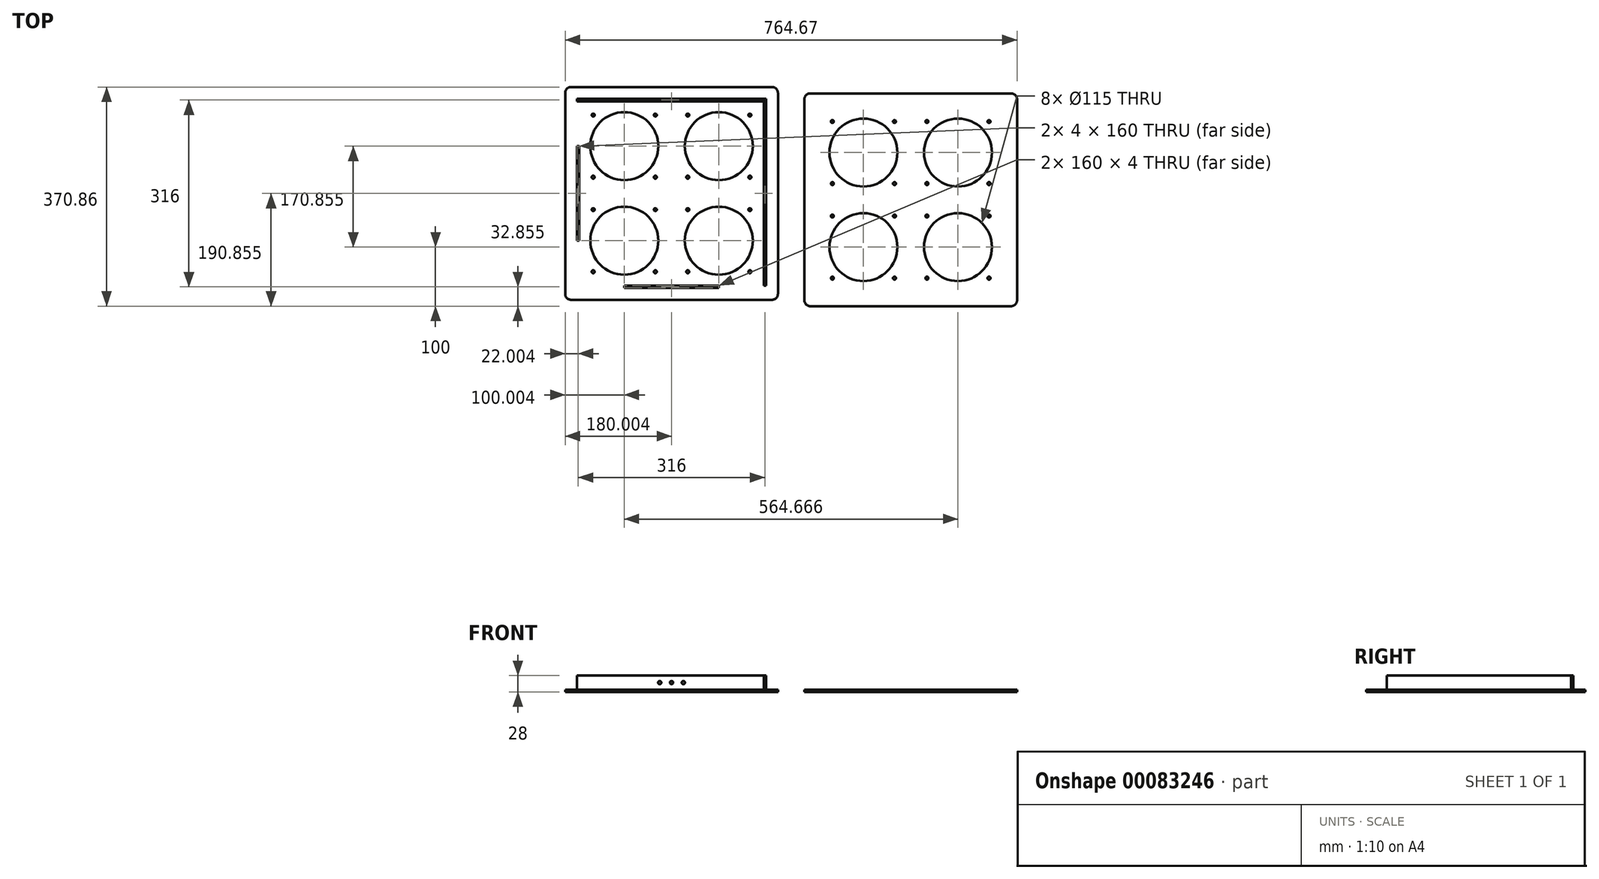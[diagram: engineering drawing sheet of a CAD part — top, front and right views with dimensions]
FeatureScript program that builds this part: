
annotation { "Feature Type Name" : "Feature", "Feature Type Description" : "" }
export const myFeature = defineFeature(function(context is Context, id is Id, definition is map)
    precondition{}
    {
        {
            var Q0;
            Q0=qCreatedBy(makeId("Top.planeOp"),FACE);
            var sketch = newSketch(context, id + "F0", { "sketchPlane" : qUnion([Q0])});
            skLineSegment(sketch, "E0.bottom", {"start": v(-180.3, 193.62) * mm, "end": v(159.7, 193.62) * mm});
            skLineSegment(sketch, "E0.top", {"start": v(-180.3, -166.38) * mm, "end": v(159.7, -166.38) * mm});
            skLineSegment(sketch, "E0.left", {"start": v(-190.3, 183.62) * mm, "end": v(-190.3, -156.38) * mm});
            skLineSegment(sketch, "E0.right", {"start": v(169.7, 183.62) * mm, "end": v(169.7, -156.38) * mm});
            skPoint(sketch, "E1.visualSharp", {"position": v(-190.3, 193.62) * mm});
            skArc(sketch, "E1.filletArc", {"start": v(-180.3, 193.62) * mm, "mid": v(-187.38, 190.69) * mm, "end": v(-190.3, 183.62) * mm});
            skPoint(sketch, "E2.visualSharp", {"position": v(169.7, 193.62) * mm});
            skArc(sketch, "E2.filletArc", {"start": v(169.7, 183.62) * mm, "mid": v(166.76, 190.69) * mm, "end": v(159.7, 193.62) * mm});
            skPoint(sketch, "E3.visualSharp", {"position": v(169.7, -166.38) * mm});
            skArc(sketch, "E3.filletArc", {"start": v(159.7, -166.38) * mm, "mid": v(166.76, -163.46) * mm, "end": v(169.7, -156.38) * mm});
            skPoint(sketch, "E4.visualSharp", {"position": v(-190.3, -166.38) * mm});
            skArc(sketch, "E4.filletArc", {"start": v(-190.3, -156.38) * mm, "mid": v(-187.38, -163.46) * mm, "end": v(-180.3, -166.38) * mm});
            skLineSegment(sketch, "E5", {"start": v(-190.3, 93.62) * mm, "end": v(169.7, 93.62) * mm, "construction": true});
            skLineSegment(sketch, "E6", {"start": v(-190.3, -66.38) * mm, "end": v(169.7, -66.38) * mm, "construction": true});
            skLineSegment(sketch, "E7", {"start": v(-90.3, 193.62) * mm, "end": v(-90.3, -166.38) * mm, "construction": true});
            skLineSegment(sketch, "E8", {"start": v(69.7, 193.62) * mm, "end": v(69.7, -166.38) * mm, "construction": true});
            skCircle(sketch, "E9", {"center": v(-90.3, 93.62) * mm, "radius": 57.5 * mm});
            skCircle(sketch, "E10", {"center": v(-90.3, 93.62) * mm, "radius": 74.3 * mm, "construction": true});
            skLineSegment(sketch, "E11.bottom", {"start": v(-30.3, 153.62) * mm, "end": v(-150.3, 153.62) * mm, "construction": true});
            skLineSegment(sketch, "E11.top", {"start": v(-30.3, 33.62) * mm, "end": v(-150.3, 33.62) * mm, "construction": true});
            skLineSegment(sketch, "E11.left", {"start": v(-30.3, 153.62) * mm, "end": v(-30.3, 33.62) * mm, "construction": true});
            skLineSegment(sketch, "E11.right", {"start": v(-150.3, 153.62) * mm, "end": v(-150.3, 33.62) * mm, "construction": true});
            skLineSegment(sketch, "E12", {"start": v(-150.3, 153.62) * mm, "end": v(-30.3, 33.62) * mm, "construction": true});
            skLineSegment(sketch, "E13", {"start": v(-150.3, 33.62) * mm, "end": v(-30.3, 153.62) * mm, "construction": true});
            skPoint(sketch, "E14", {"position": v(-142.84, 146.15) * mm});
            skPoint(sketch, "E15", {"position": v(-37.77, 146.15) * mm});
            skPoint(sketch, "E16", {"position": v(-37.77, 41.08) * mm});
            skPoint(sketch, "E17", {"position": v(-142.84, 41.08) * mm});
            skCircle(sketch, "E18", {"center": v(-142.84, 146.15) * mm, "radius": 2.5 * mm});
            skCircle(sketch, "E19", {"center": v(-37.77, 146.15) * mm, "radius": 2.5 * mm});
            skCircle(sketch, "E20", {"center": v(-37.77, 41.08) * mm, "radius": 2.5 * mm});
            skCircle(sketch, "E21", {"center": v(-142.84, 41.08) * mm, "radius": 2.5 * mm});
            skLineSegment(sketch, "E22", {"start": v(-190.3, 13.62) * mm, "end": v(169.7, 13.62) * mm, "construction": true});
            skLineSegment(sketch, "E23", {"start": v(-10.3, 193.62) * mm, "end": v(-10.3, -166.38) * mm, "construction": true});
            skLineSegment(sketch, "E24.0.1.0", {"start": v(-30.3, -6.38) * mm, "end": v(-150.3, -6.38) * mm, "construction": true});
            skLineSegment(sketch, "E24.0.1.1", {"start": v(-30.3, -126.38) * mm, "end": v(-150.3, -126.38) * mm, "construction": true});
            skPoint(sketch, "E24.0.1.2", {"position": v(-90.3, -66.38) * mm});
            skCircle(sketch, "E24.0.1.3", {"center": v(-90.3, -66.38) * mm, "radius": 57.5 * mm});
            skPoint(sketch, "E24.0.1.4", {"position": v(-37.77, -13.85) * mm});
            skCircle(sketch, "E24.0.1.5", {"center": v(-90.3, -66.38) * mm, "radius": 74.3 * mm, "construction": true});
            skLineSegment(sketch, "E24.0.1.6", {"start": v(-30.3, -6.38) * mm, "end": v(-30.3, -126.38) * mm, "construction": true});
            skLineSegment(sketch, "E24.0.1.7", {"start": v(-150.3, -6.38) * mm, "end": v(-30.3, -126.38) * mm, "construction": true});
            skLineSegment(sketch, "E24.0.1.8", {"start": v(-150.3, -6.38) * mm, "end": v(-150.3, -126.38) * mm, "construction": true});
            skLineSegment(sketch, "E24.0.1.9", {"start": v(-150.3, -126.38) * mm, "end": v(-30.3, -6.38) * mm, "construction": true});
            skPoint(sketch, "E24.0.1.10", {"position": v(-142.84, -118.92) * mm});
            skPoint(sketch, "E24.0.1.11", {"position": v(-142.84, -13.85) * mm});
            skPoint(sketch, "E24.0.1.12", {"position": v(-37.77, -118.92) * mm});
            skPoint(sketch, "E24.0.1.13", {"position": v(-90.3, -66.38) * mm});
            skCircle(sketch, "E24.0.1.14", {"center": v(-142.84, -118.92) * mm, "radius": 2.5 * mm});
            skCircle(sketch, "E24.0.1.15", {"center": v(-37.77, -118.92) * mm, "radius": 2.5 * mm});
            skCircle(sketch, "E24.0.1.16", {"center": v(-142.84, -13.85) * mm, "radius": 2.5 * mm});
            skCircle(sketch, "E24.0.1.17", {"center": v(-37.77, -13.85) * mm, "radius": 2.5 * mm});
            skLineSegment(sketch, "E24.1.0.0", {"start": v(129.7, 153.62) * mm, "end": v(9.7, 153.62) * mm, "construction": true});
            skLineSegment(sketch, "E24.1.0.1", {"start": v(129.7, 33.62) * mm, "end": v(9.7, 33.62) * mm, "construction": true});
            skPoint(sketch, "E24.1.0.2", {"position": v(69.7, 93.62) * mm});
            skCircle(sketch, "E24.1.0.3", {"center": v(69.7, 93.62) * mm, "radius": 57.5 * mm});
            skPoint(sketch, "E24.1.0.4", {"position": v(122.23, 146.15) * mm});
            skCircle(sketch, "E24.1.0.5", {"center": v(69.7, 93.62) * mm, "radius": 74.3 * mm, "construction": true});
            skLineSegment(sketch, "E24.1.0.6", {"start": v(129.7, 153.62) * mm, "end": v(129.7, 33.62) * mm, "construction": true});
            skLineSegment(sketch, "E24.1.0.7", {"start": v(9.7, 153.62) * mm, "end": v(129.7, 33.62) * mm, "construction": true});
            skLineSegment(sketch, "E24.1.0.8", {"start": v(9.7, 153.62) * mm, "end": v(9.7, 33.62) * mm, "construction": true});
            skLineSegment(sketch, "E24.1.0.9", {"start": v(9.7, 33.62) * mm, "end": v(129.7, 153.62) * mm, "construction": true});
            skPoint(sketch, "E24.1.0.10", {"position": v(17.16, 41.08) * mm});
            skPoint(sketch, "E24.1.0.11", {"position": v(17.16, 146.15) * mm});
            skPoint(sketch, "E24.1.0.12", {"position": v(122.23, 41.08) * mm});
            skPoint(sketch, "E24.1.0.13", {"position": v(69.7, 93.62) * mm});
            skCircle(sketch, "E24.1.0.14", {"center": v(17.16, 41.08) * mm, "radius": 2.5 * mm});
            skCircle(sketch, "E24.1.0.15", {"center": v(122.23, 41.08) * mm, "radius": 2.5 * mm});
            skCircle(sketch, "E24.1.0.16", {"center": v(17.16, 146.15) * mm, "radius": 2.5 * mm});
            skCircle(sketch, "E24.1.0.17", {"center": v(122.23, 146.15) * mm, "radius": 2.5 * mm});
            skLineSegment(sketch, "E24.1.1.0", {"start": v(129.7, -6.38) * mm, "end": v(9.7, -6.38) * mm, "construction": true});
            skLineSegment(sketch, "E24.1.1.1", {"start": v(129.7, -126.38) * mm, "end": v(9.7, -126.38) * mm, "construction": true});
            skPoint(sketch, "E24.1.1.2", {"position": v(69.7, -66.38) * mm});
            skCircle(sketch, "E24.1.1.3", {"center": v(69.7, -66.38) * mm, "radius": 57.5 * mm});
            skPoint(sketch, "E24.1.1.4", {"position": v(122.23, -13.85) * mm});
            skCircle(sketch, "E24.1.1.5", {"center": v(69.7, -66.38) * mm, "radius": 74.3 * mm, "construction": true});
            skLineSegment(sketch, "E24.1.1.6", {"start": v(129.7, -6.38) * mm, "end": v(129.7, -126.38) * mm, "construction": true});
            skLineSegment(sketch, "E24.1.1.7", {"start": v(9.7, -6.38) * mm, "end": v(129.7, -126.38) * mm, "construction": true});
            skLineSegment(sketch, "E24.1.1.8", {"start": v(9.7, -6.38) * mm, "end": v(9.7, -126.38) * mm, "construction": true});
            skLineSegment(sketch, "E24.1.1.9", {"start": v(9.7, -126.38) * mm, "end": v(129.7, -6.38) * mm, "construction": true});
            skPoint(sketch, "E24.1.1.10", {"position": v(17.16, -118.92) * mm});
            skPoint(sketch, "E24.1.1.11", {"position": v(17.16, -13.85) * mm});
            skPoint(sketch, "E24.1.1.12", {"position": v(122.23, -118.92) * mm});
            skPoint(sketch, "E24.1.1.13", {"position": v(69.7, -66.38) * mm});
            skCircle(sketch, "E24.1.1.14", {"center": v(17.16, -118.92) * mm, "radius": 2.5 * mm});
            skCircle(sketch, "E24.1.1.15", {"center": v(122.23, -118.92) * mm, "radius": 2.5 * mm});
            skCircle(sketch, "E24.1.1.16", {"center": v(17.16, -13.85) * mm, "radius": 2.5 * mm});
            skCircle(sketch, "E24.1.1.17", {"center": v(122.23, -13.85) * mm, "radius": 2.5 * mm});
            skLineSegment(sketch, "E24.direction1", {"start": v(-150.3, 33.62) * mm, "end": v(9.7, 33.62) * mm, "construction": true});
            skLineSegment(sketch, "E24.direction2", {"start": v(-150.3, 33.62) * mm, "end": v(-150.3, -126.38) * mm, "construction": true});
            skLineSegment(sketch, "E25", {"start": v(-166.3, 93.62) * mm, "end": v(-166.3, -66.38) * mm});
            skLineSegment(sketch, "E26", {"start": v(-170.3, 93.62) * mm, "end": v(-170.3, -66.38) * mm});
            skLineSegment(sketch, "E27", {"start": v(-170.3, 93.62) * mm, "end": v(-166.3, 93.62) * mm});
            skLineSegment(sketch, "E28", {"start": v(-170.3, -66.38) * mm, "end": v(-166.3, -66.38) * mm});
            skLineSegment(sketch, "E29.bottom", {"start": v(-90.3, -146.38) * mm, "end": v(69.7, -146.38) * mm});
            skLineSegment(sketch, "E29.top", {"start": v(-90.3, -142.38) * mm, "end": v(69.7, -142.38) * mm});
            skLineSegment(sketch, "E29.left", {"start": v(-90.3, -146.38) * mm, "end": v(-90.3, -142.38) * mm});
            skLineSegment(sketch, "E29.right", {"start": v(69.7, -146.38) * mm, "end": v(69.7, -142.38) * mm});
            skLineSegment(sketch, "E30.MirrorCS", {"start": v(-90.3, 173.62) * mm, "end": v(-90.3, 169.62) * mm});
            skLineSegment(sketch, "E31.MirrorCS", {"start": v(69.7, 173.62) * mm, "end": v(69.7, 169.62) * mm});
            skLineSegment(sketch, "E32.MirrorCS", {"start": v(-90.3, 173.62) * mm, "end": v(69.7, 173.62) * mm});
            skLineSegment(sketch, "E33.MirrorCS", {"start": v(-90.3, 169.62) * mm, "end": v(69.7, 169.62) * mm});
            skLineSegment(sketch, "E34.MirrorCS", {"start": v(149.7, -66.38) * mm, "end": v(145.7, -66.38) * mm});
            skLineSegment(sketch, "E35.MirrorCS", {"start": v(149.7, 93.62) * mm, "end": v(145.7, 93.62) * mm});
            skLineSegment(sketch, "E36.MirrorCS", {"start": v(149.7, 93.62) * mm, "end": v(149.7, -66.38) * mm});
            skLineSegment(sketch, "E37.MirrorCS", {"start": v(145.7, 93.62) * mm, "end": v(145.7, -66.38) * mm});
            skLineSegment(sketch, "E38.bottom", {"start": v(224.36, 182.76) * mm, "end": v(564.36, 182.76) * mm});
            skLineSegment(sketch, "E38.top", {"start": v(224.36, -177.24) * mm, "end": v(564.36, -177.24) * mm});
            skLineSegment(sketch, "E38.left", {"start": v(214.36, 172.76) * mm, "end": v(214.36, -167.24) * mm});
            skLineSegment(sketch, "E38.right", {"start": v(574.36, 172.76) * mm, "end": v(574.36, -167.24) * mm});
            skPoint(sketch, "E39.visualSharp", {"position": v(214.36, 182.76) * mm});
            skArc(sketch, "E39.filletArc", {"start": v(224.36, 182.76) * mm, "mid": v(217.29, 179.83) * mm, "end": v(214.36, 172.76) * mm});
            skPoint(sketch, "E40.visualSharp", {"position": v(574.36, 182.76) * mm});
            skArc(sketch, "E40.filletArc", {"start": v(574.36, 172.76) * mm, "mid": v(571.43, 179.83) * mm, "end": v(564.36, 182.76) * mm});
            skPoint(sketch, "E41.visualSharp", {"position": v(574.36, -177.24) * mm});
            skArc(sketch, "E41.filletArc", {"start": v(564.36, -177.24) * mm, "mid": v(571.43, -174.31) * mm, "end": v(574.36, -167.24) * mm});
            skPoint(sketch, "E42.visualSharp", {"position": v(214.36, -177.24) * mm});
            skArc(sketch, "E42.filletArc", {"start": v(214.36, -167.24) * mm, "mid": v(217.29, -174.31) * mm, "end": v(224.36, -177.24) * mm});
            skLineSegment(sketch, "E43", {"start": v(214.36, 82.76) * mm, "end": v(574.36, 82.76) * mm, "construction": true});
            skLineSegment(sketch, "E44", {"start": v(214.36, -77.24) * mm, "end": v(574.36, -77.24) * mm, "construction": true});
            skLineSegment(sketch, "E45", {"start": v(314.36, 182.76) * mm, "end": v(314.36, -177.24) * mm, "construction": true});
            skLineSegment(sketch, "E46", {"start": v(474.36, 182.76) * mm, "end": v(474.36, -177.24) * mm, "construction": true});
            skCircle(sketch, "E47", {"center": v(314.36, 82.76) * mm, "radius": 57.5 * mm});
            skCircle(sketch, "E48", {"center": v(314.36, 82.76) * mm, "radius": 74.3 * mm, "construction": true});
            skLineSegment(sketch, "E49.bottom", {"start": v(374.36, 142.76) * mm, "end": v(254.36, 142.76) * mm, "construction": true});
            skLineSegment(sketch, "E49.top", {"start": v(374.36, 22.76) * mm, "end": v(254.36, 22.76) * mm, "construction": true});
            skLineSegment(sketch, "E49.left", {"start": v(374.36, 142.76) * mm, "end": v(374.36, 22.76) * mm, "construction": true});
            skLineSegment(sketch, "E49.right", {"start": v(254.36, 142.76) * mm, "end": v(254.36, 22.76) * mm, "construction": true});
            skLineSegment(sketch, "E50", {"start": v(254.36, 142.76) * mm, "end": v(374.36, 22.76) * mm, "construction": true});
            skLineSegment(sketch, "E51", {"start": v(254.36, 22.76) * mm, "end": v(374.36, 142.76) * mm, "construction": true});
            skPoint(sketch, "E52", {"position": v(261.82, 135.3) * mm});
            skPoint(sketch, "E53", {"position": v(366.9, 135.3) * mm});
            skPoint(sketch, "E54", {"position": v(366.9, 30.22) * mm});
            skPoint(sketch, "E55", {"position": v(261.82, 30.22) * mm});
            skCircle(sketch, "E56", {"center": v(261.82, 135.3) * mm, "radius": 2.5 * mm});
            skCircle(sketch, "E57", {"center": v(366.9, 135.3) * mm, "radius": 2.5 * mm});
            skCircle(sketch, "E58", {"center": v(366.9, 30.22) * mm, "radius": 2.5 * mm});
            skCircle(sketch, "E59", {"center": v(261.82, 30.22) * mm, "radius": 2.5 * mm});
            skLineSegment(sketch, "E60", {"start": v(214.36, 2.76) * mm, "end": v(574.36, 2.76) * mm, "construction": true});
            skLineSegment(sketch, "E61", {"start": v(394.36, 182.76) * mm, "end": v(394.36, -177.24) * mm, "construction": true});
            skLineSegment(sketch, "E62.0.1.0", {"start": v(374.36, -17.24) * mm, "end": v(254.36, -17.24) * mm, "construction": true});
            skLineSegment(sketch, "E62.0.1.1", {"start": v(374.36, -137.24) * mm, "end": v(254.36, -137.24) * mm, "construction": true});
            skPoint(sketch, "E62.0.1.2", {"position": v(314.36, -77.24) * mm});
            skCircle(sketch, "E62.0.1.3", {"center": v(314.36, -77.24) * mm, "radius": 57.5 * mm});
            skPoint(sketch, "E62.0.1.4", {"position": v(366.9, -24.7) * mm});
            skCircle(sketch, "E62.0.1.5", {"center": v(314.36, -77.24) * mm, "radius": 74.3 * mm, "construction": true});
            skLineSegment(sketch, "E62.0.1.6", {"start": v(374.36, -17.24) * mm, "end": v(374.36, -137.24) * mm, "construction": true});
            skLineSegment(sketch, "E62.0.1.7", {"start": v(254.36, -17.24) * mm, "end": v(374.36, -137.24) * mm, "construction": true});
            skLineSegment(sketch, "E62.0.1.8", {"start": v(254.36, -17.24) * mm, "end": v(254.36, -137.24) * mm, "construction": true});
            skLineSegment(sketch, "E62.0.1.9", {"start": v(254.36, -137.24) * mm, "end": v(374.36, -17.24) * mm, "construction": true});
            skPoint(sketch, "E62.0.1.10", {"position": v(261.82, -129.78) * mm});
            skPoint(sketch, "E62.0.1.11", {"position": v(261.82, -24.7) * mm});
            skPoint(sketch, "E62.0.1.12", {"position": v(366.9, -129.78) * mm});
            skPoint(sketch, "E62.0.1.13", {"position": v(314.36, -77.24) * mm});
            skCircle(sketch, "E62.0.1.14", {"center": v(261.82, -129.78) * mm, "radius": 2.5 * mm});
            skCircle(sketch, "E62.0.1.15", {"center": v(366.9, -129.78) * mm, "radius": 2.5 * mm});
            skCircle(sketch, "E62.0.1.16", {"center": v(261.82, -24.7) * mm, "radius": 2.5 * mm});
            skCircle(sketch, "E62.0.1.17", {"center": v(366.9, -24.7) * mm, "radius": 2.5 * mm});
            skLineSegment(sketch, "E62.1.0.0", {"start": v(534.36, 142.76) * mm, "end": v(414.36, 142.76) * mm, "construction": true});
            skLineSegment(sketch, "E62.1.0.1", {"start": v(534.36, 22.76) * mm, "end": v(414.36, 22.76) * mm, "construction": true});
            skPoint(sketch, "E62.1.0.2", {"position": v(474.36, 82.76) * mm});
            skCircle(sketch, "E62.1.0.3", {"center": v(474.36, 82.76) * mm, "radius": 57.5 * mm});
            skPoint(sketch, "E62.1.0.4", {"position": v(526.9, 135.3) * mm});
            skCircle(sketch, "E62.1.0.5", {"center": v(474.36, 82.76) * mm, "radius": 74.3 * mm, "construction": true});
            skLineSegment(sketch, "E62.1.0.6", {"start": v(534.36, 142.76) * mm, "end": v(534.36, 22.76) * mm, "construction": true});
            skLineSegment(sketch, "E62.1.0.7", {"start": v(414.36, 142.76) * mm, "end": v(534.36, 22.76) * mm, "construction": true});
            skLineSegment(sketch, "E62.1.0.8", {"start": v(414.36, 142.76) * mm, "end": v(414.36, 22.76) * mm, "construction": true});
            skLineSegment(sketch, "E62.1.0.9", {"start": v(414.36, 22.76) * mm, "end": v(534.36, 142.76) * mm, "construction": true});
            skPoint(sketch, "E62.1.0.10", {"position": v(421.82, 30.22) * mm});
            skPoint(sketch, "E62.1.0.11", {"position": v(421.82, 135.3) * mm});
            skPoint(sketch, "E62.1.0.12", {"position": v(526.9, 30.22) * mm});
            skPoint(sketch, "E62.1.0.13", {"position": v(474.36, 82.76) * mm});
            skCircle(sketch, "E62.1.0.14", {"center": v(421.82, 30.22) * mm, "radius": 2.5 * mm});
            skCircle(sketch, "E62.1.0.15", {"center": v(526.9, 30.22) * mm, "radius": 2.5 * mm});
            skCircle(sketch, "E62.1.0.16", {"center": v(421.82, 135.3) * mm, "radius": 2.5 * mm});
            skCircle(sketch, "E62.1.0.17", {"center": v(526.9, 135.3) * mm, "radius": 2.5 * mm});
            skLineSegment(sketch, "E62.1.1.0", {"start": v(534.36, -17.24) * mm, "end": v(414.36, -17.24) * mm, "construction": true});
            skLineSegment(sketch, "E62.1.1.1", {"start": v(534.36, -137.24) * mm, "end": v(414.36, -137.24) * mm, "construction": true});
            skPoint(sketch, "E62.1.1.2", {"position": v(474.36, -77.24) * mm});
            skCircle(sketch, "E62.1.1.3", {"center": v(474.36, -77.24) * mm, "radius": 57.5 * mm});
            skPoint(sketch, "E62.1.1.4", {"position": v(526.9, -24.7) * mm});
            skCircle(sketch, "E62.1.1.5", {"center": v(474.36, -77.24) * mm, "radius": 74.3 * mm, "construction": true});
            skLineSegment(sketch, "E62.1.1.6", {"start": v(534.36, -17.24) * mm, "end": v(534.36, -137.24) * mm, "construction": true});
            skLineSegment(sketch, "E62.1.1.7", {"start": v(414.36, -17.24) * mm, "end": v(534.36, -137.24) * mm, "construction": true});
            skLineSegment(sketch, "E62.1.1.8", {"start": v(414.36, -17.24) * mm, "end": v(414.36, -137.24) * mm, "construction": true});
            skLineSegment(sketch, "E62.1.1.9", {"start": v(414.36, -137.24) * mm, "end": v(534.36, -17.24) * mm, "construction": true});
            skPoint(sketch, "E62.1.1.10", {"position": v(421.82, -129.78) * mm});
            skPoint(sketch, "E62.1.1.11", {"position": v(421.82, -24.7) * mm});
            skPoint(sketch, "E62.1.1.12", {"position": v(526.9, -129.78) * mm});
            skPoint(sketch, "E62.1.1.13", {"position": v(474.36, -77.24) * mm});
            skCircle(sketch, "E62.1.1.14", {"center": v(421.82, -129.78) * mm, "radius": 2.5 * mm});
            skCircle(sketch, "E62.1.1.15", {"center": v(526.9, -129.78) * mm, "radius": 2.5 * mm});
            skCircle(sketch, "E62.1.1.16", {"center": v(421.82, -24.7) * mm, "radius": 2.5 * mm});
            skCircle(sketch, "E62.1.1.17", {"center": v(526.9, -24.7) * mm, "radius": 2.5 * mm});
            skLineSegment(sketch, "E62.direction1", {"start": v(254.36, 22.76) * mm, "end": v(414.36, 22.76) * mm, "construction": true});
            skLineSegment(sketch, "E62.direction2", {"start": v(254.36, 22.76) * mm, "end": v(254.36, -137.24) * mm, "construction": true});
            skSolve(sketch);
        }
        {
            var Q0;
            Q0=makeQuery(id+"F0.imprint","IMPRINT",FACE,{"disambiguationData":[TD([[makeQuery(id+"F0.imprint","IMPRINT",EDGE,{"derivedFrom":sQuery(id+"F0.wireOp",EDGE,"E0.bottom")}),-1.0]])]});
            var Q1;
            Q1=makeQuery(id+"F0.imprint","IMPRINT",FACE,{"disambiguationData":[TD([[makeQuery(id+"F0.imprint","IMPRINT",EDGE,{"derivedFrom":sQuery(id+"F0.wireOp",EDGE,"E38.bottom")}),-1.0]])]});
            extrude(context, id + "F1", {"entities" : qUnion([Q0, Q1]), "depth" : 4 * mm});
        }
        {
            var Q0;
            Q0=makeQuery(id+"F1.opExtrude","SWEPT_FACE",FACE,{"disambiguationData":[OSD([sQuery(id+"F0.wireOp",EDGE,"E32.MirrorCS")])]});
            var sketch = newSketch(context, id + "F2", { "sketchPlane" : qUnion([Q0])});
            skPoint(sketch, "E63.0", {"position": v(-90.3, 0) * mm});
            skPoint(sketch, "E64.0", {"position": v(-90.3, 4) * mm});
            skPoint(sketch, "E65.0", {"position": v(69.7, 0) * mm});
            skPoint(sketch, "E66.0", {"position": v(69.7, 4) * mm});
            skPoint(sketch, "E67.0", {"position": v(149.7, 4) * mm});
            skPoint(sketch, "E68.0", {"position": v(-170.3, 4) * mm});
            skLineSegment(sketch, "E69", {"start": v(-90.3, 0) * mm, "end": v(-90.3, 4) * mm});
            skLineSegment(sketch, "E70", {"start": v(-170.3, 4) * mm, "end": v(-170.3, 28) * mm});
            skLineSegment(sketch, "E71", {"start": v(-170.3, 28) * mm, "end": v(149.7, 28) * mm});
            skLineSegment(sketch, "E72", {"start": v(149.7, 28) * mm, "end": v(149.7, 4) * mm});
            skLineSegment(sketch, "E73", {"start": v(69.7, 4) * mm, "end": v(69.7, 0) * mm});
            skLineSegment(sketch, "E74", {"start": v(-90.3, 0) * mm, "end": v(69.7, 0) * mm});
            skLineSegment(sketch, "E75", {"start": v(69.7, 0) * mm, "end": v(69.7, 4) * mm});
            skLineSegment(sketch, "E76", {"start": v(69.7, 4) * mm, "end": v(149.7, 4) * mm});
            skLineSegment(sketch, "E77", {"start": v(-90.3, 4) * mm, "end": v(-170.3, 4) * mm});
            skLineSegment(sketch, "E78", {"start": v(-170.3, 16) * mm, "end": v(149.7, 16) * mm, "construction": true});
            skLineSegment(sketch, "E79", {"start": v(-10.3, 28) * mm, "end": v(-10.3, 4) * mm, "construction": true});
            skCircle(sketch, "E80", {"center": v(-10.3, 16) * mm, "radius": 2.75 * mm});
            skCircle(sketch, "E81", {"center": v(-30.3, 16) * mm, "radius": 2.75 * mm});
            skCircle(sketch, "E82", {"center": v(9.7, 16) * mm, "radius": 2.75 * mm});
            skSolve(sketch);
        }
        {
            var Q0;
            Q0=makeQuery(id+"F2.imprint","IMPRINT",FACE,{"disambiguationData":[TD([[makeQuery(id+"F2.imprint","IMPRINT",EDGE,{"derivedFrom":sQuery(id+"F2.wireOp",EDGE,"E70")}),-1.0]])]});
            var Q1;
            Q1=makeQuery(id+"F2.imprint","IMPRINT",FACE,{"disambiguationData":[TD([[makeQuery(id+"F2.imprint","IMPRINT",EDGE,{"derivedFrom":sQuery(id+"F2.wireOp",EDGE,"E69")}),1.0]])]});
            extrude(context, id + "F3", {"entities" : qUnion([Q0, Q1]), "depth" : 4 * mm});
        }
        {
            var Q0;
            Q0=makeQuery(id+"F1.opExtrude","SWEPT_FACE",FACE,{"disambiguationData":[OSD([sQuery(id+"F0.wireOp",EDGE,"E36.MirrorCS")])]});
            var sketch = newSketch(context, id + "F4", { "sketchPlane" : qUnion([Q0])});
            skPoint(sketch, "E83.0", {"position": v(-93.62, 0) * mm});
            skPoint(sketch, "E84.0", {"position": v(-93.62, 4) * mm});
            skPoint(sketch, "E85.0", {"position": v(66.38, 0) * mm});
            skPoint(sketch, "E86.0", {"position": v(66.38, 4) * mm});
            skPoint(sketch, "E87.0", {"position": v(-169.62, 4) * mm});
            skPoint(sketch, "E88.0", {"position": v(142.38, 4) * mm});
            skLineSegment(sketch, "E89", {"start": v(-93.62, 0) * mm, "end": v(-93.62, 4) * mm});
            skLineSegment(sketch, "E90", {"start": v(-93.62, 4) * mm, "end": v(-169.62, 4) * mm});
            skLineSegment(sketch, "E91", {"start": v(-169.62, 4) * mm, "end": v(-169.62, 28) * mm});
            skLineSegment(sketch, "E92", {"start": v(142.38, 4) * mm, "end": v(66.38, 4) * mm});
            skLineSegment(sketch, "E93", {"start": v(66.38, 4) * mm, "end": v(66.38, 0) * mm});
            skLineSegment(sketch, "E94", {"start": v(66.38, 0) * mm, "end": v(-93.62, 0) * mm});
            skLineSegment(sketch, "E95", {"start": v(-169.62, 28) * mm, "end": v(142.38, 28) * mm});
            skLineSegment(sketch, "E96", {"start": v(142.38, 28) * mm, "end": v(142.38, 4) * mm});
            skSolve(sketch);
        }
        {
            var Q0;
            Q0=makeQuery(id+"F4.imprint","IMPRINT",FACE,{"disambiguationData":[TD([[makeQuery(id+"F4.imprint","IMPRINT",EDGE,{"derivedFrom":sQuery(id+"F4.wireOp",EDGE,"E90")}),-1.0]])]});
            var Q1;
            Q1=makeQuery(id+"F4.imprint","IMPRINT",FACE,{"disambiguationData":[TD([[makeQuery(id+"F4.imprint","IMPRINT",EDGE,{"derivedFrom":sQuery(id+"F4.wireOp",EDGE,"E89")}),1.0]])]});
            extrude(context, id + "F5", {"entities" : qUnion([Q0, Q1]), "depth" : 4 * mm});
        }
    });
